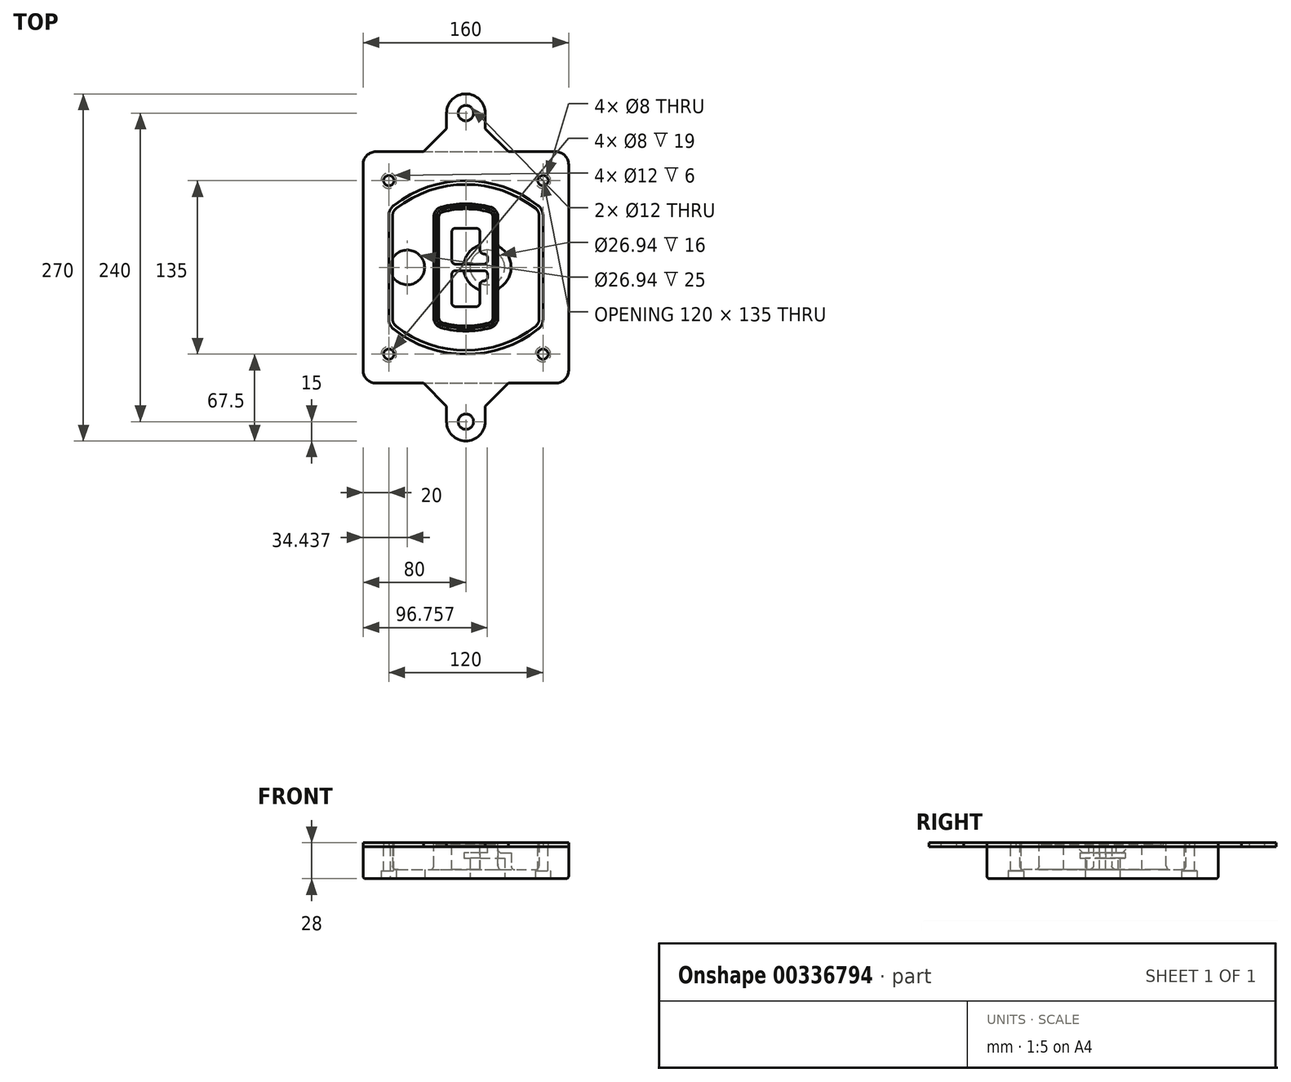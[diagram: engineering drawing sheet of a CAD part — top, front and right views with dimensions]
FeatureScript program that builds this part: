
annotation { "Feature Type Name" : "Feature", "Feature Type Description" : "" }
export const myFeature = defineFeature(function(context is Context, id is Id, definition is map)
    precondition{}
    {
        {
            var Q0;
            Q0=qCreatedBy(makeId("Top.planeOp"),FACE);
            var sketch = newSketch(context, id + "F0", { "sketchPlane" : qUnion([Q0])});
            skPoint(sketch, "E0.rect.middle", {"position": v(0, 0) * mm});
            skLineSegment(sketch, "E1.bottom", {"start": v(-70, -90) * mm, "end": v(70, -90) * mm});
            skLineSegment(sketch, "E1.top", {"start": v(-70, 90) * mm, "end": v(70, 90) * mm});
            skLineSegment(sketch, "E1.left", {"start": v(-80, -80) * mm, "end": v(-80, 80) * mm});
            skLineSegment(sketch, "E1.right", {"start": v(80, -80) * mm, "end": v(80, 80) * mm});
            skLineSegment(sketch, "E2", {"start": v(-80, 90) * mm, "end": v(80, -90) * mm, "construction": true});
            skLineSegment(sketch, "E3", {"start": v(80, 90) * mm, "end": v(-80, -90) * mm, "construction": true});
            skCircle(sketch, "E4", {"center": v(-60, 67.5) * mm, "radius": 4 * mm});
            skCircle(sketch, "E5", {"center": v(60, 67.5) * mm, "radius": 4 * mm});
            skCircle(sketch, "E6", {"center": v(60, -67.5) * mm, "radius": 4 * mm});
            skCircle(sketch, "E7", {"center": v(-60, -67.5) * mm, "radius": 4 * mm});
            skLineSegment(sketch, "E8", {"start": v(-60, 67.5) * mm, "end": v(60, 67.5) * mm, "construction": true});
            skLineSegment(sketch, "E9", {"start": v(60, 67.5) * mm, "end": v(60, -67.5) * mm, "construction": true});
            skLineSegment(sketch, "E10", {"start": v(60, -67.5) * mm, "end": v(-60, -67.5) * mm, "construction": true});
            skLineSegment(sketch, "E11", {"start": v(-60, -67.5) * mm, "end": v(-60, 67.5) * mm, "construction": true});
            skLineSegment(sketch, "E12", {"start": v(-60, 40.3) * mm, "end": v(-60, -40.3) * mm});
            skLineSegment(sketch, "E13", {"start": v(60, 40.3) * mm, "end": v(60, -40.3) * mm});
            skArc(sketch, "E14", {"start": v(56.15, 48.18) * mm, "mid": v(0, 67.5) * mm, "end": v(-56.15, 48.18) * mm});
            skArc(sketch, "E15", {"start": v(-56.15, -48.18) * mm, "mid": v(0, -67.5) * mm, "end": v(56.15, -48.18) * mm});
            skLineSegment(sketch, "E16", {"start": v(-60, 0) * mm, "end": v(60, 0) * mm, "construction": true});
            skPoint(sketch, "E17.visualSharp", {"position": v(-60, -45) * mm});
            skArc(sketch, "E17.filletArc", {"start": v(-60, -40.3) * mm, "mid": v(-58.99, -44.68) * mm, "end": v(-56.15, -48.18) * mm});
            skPoint(sketch, "E18.visualSharp", {"position": v(-60, 45) * mm});
            skArc(sketch, "E18.filletArc", {"start": v(-56.15, 48.18) * mm, "mid": v(-58.99, 44.68) * mm, "end": v(-60, 40.3) * mm});
            skPoint(sketch, "E19.visualSharp", {"position": v(60, 45) * mm});
            skArc(sketch, "E19.filletArc", {"start": v(60, 40.3) * mm, "mid": v(58.99, 44.68) * mm, "end": v(56.15, 48.18) * mm});
            skPoint(sketch, "E20.visualSharp", {"position": v(60, -45) * mm});
            skArc(sketch, "E20.filletArc", {"start": v(56.15, -48.18) * mm, "mid": v(58.99, -44.68) * mm, "end": v(60, -40.3) * mm});
            skPoint(sketch, "E21.visualSharp", {"position": v(-80, 90) * mm});
            skArc(sketch, "E21.filletArc", {"start": v(-70, 90) * mm, "mid": v(-77.07, 87.07) * mm, "end": v(-80, 80) * mm});
            skPoint(sketch, "E22.visualSharp", {"position": v(80, 90) * mm});
            skArc(sketch, "E22.filletArc", {"start": v(80, 80) * mm, "mid": v(77.07, 87.07) * mm, "end": v(70, 90) * mm});
            skPoint(sketch, "E23.visualSharp", {"position": v(80, -90) * mm});
            skArc(sketch, "E23.filletArc", {"start": v(70, -90) * mm, "mid": v(77.07, -87.07) * mm, "end": v(80, -80) * mm});
            skPoint(sketch, "E24.visualSharp", {"position": v(-80, -90) * mm});
            skArc(sketch, "E24.filletArc", {"start": v(-80, -80) * mm, "mid": v(-77.07, -87.07) * mm, "end": v(-70, -90) * mm});
            skArc(sketch, "E25.0", {"start": v(57, 40.3) * mm, "mid": v(56.3, 43.36) * mm, "end": v(54.3, 45.81) * mm});
            skLineSegment(sketch, "E25.1", {"start": v(57, 40.3) * mm, "end": v(57, -40.3) * mm});
            skArc(sketch, "E25.2", {"start": v(54.3, -45.81) * mm, "mid": v(56.3, -43.36) * mm, "end": v(57, -40.3) * mm});
            skArc(sketch, "E25.3", {"start": v(-54.3, -45.81) * mm, "mid": v(0, -64.5) * mm, "end": v(54.3, -45.81) * mm});
            skArc(sketch, "E25.4", {"start": v(-57, -40.3) * mm, "mid": v(-56.3, -43.36) * mm, "end": v(-54.3, -45.81) * mm});
            skArc(sketch, "E25.5", {"start": v(54.3, 45.81) * mm, "mid": v(0, 64.5) * mm, "end": v(-54.3, 45.81) * mm});
            skLineSegment(sketch, "E25.6", {"start": v(-57, 40.3) * mm, "end": v(-57, -40.3) * mm});
            skArc(sketch, "E25.7", {"start": v(-54.3, 45.81) * mm, "mid": v(-56.3, 43.36) * mm, "end": v(-57, 40.3) * mm});
            skArc(sketch, "E26.0", {"start": v(-58.62, 51.33) * mm, "mid": v(-62.58, 46.43) * mm, "end": v(-64, 40.3) * mm});
            skArc(sketch, "E26.1", {"start": v(58.62, 51.33) * mm, "mid": v(0, 71.5) * mm, "end": v(-58.62, 51.33) * mm});
            skArc(sketch, "E26.2", {"start": v(64, 40.3) * mm, "mid": v(62.58, 46.43) * mm, "end": v(58.62, 51.33) * mm});
            skLineSegment(sketch, "E26.3", {"start": v(64, 40.3) * mm, "end": v(64, -40.3) * mm});
            skArc(sketch, "E26.4", {"start": v(58.62, -51.33) * mm, "mid": v(62.58, -46.43) * mm, "end": v(64, -40.3) * mm});
            skLineSegment(sketch, "E26.5", {"start": v(-64, 40.3) * mm, "end": v(-64, -40.3) * mm});
            skArc(sketch, "E26.6", {"start": v(-58.62, -51.33) * mm, "mid": v(0, -71.5) * mm, "end": v(58.62, -51.33) * mm});
            skArc(sketch, "E26.7", {"start": v(-64, -40.3) * mm, "mid": v(-62.58, -46.43) * mm, "end": v(-58.62, -51.33) * mm});
            skSolve(sketch);
        }
        {
            var Q0;
            Q0=makeQuery(id+"F0.imprint","IMPRINT",FACE,{"disambiguationData":[TD([[makeQuery(id+"F0.imprint","IMPRINT",EDGE,{"derivedFrom":sQuery(id+"F0.wireOp",EDGE,"E1.bottom")}),1.0]])]});
            var Q1;
            Q1=makeQuery(id+"F0.imprint","IMPRINT",FACE,{"disambiguationData":[TD([[makeQuery(id+"F0.imprint","IMPRINT",EDGE,{"derivedFrom":sQuery(id+"F0.wireOp",EDGE,"E12")}),1.0]])]});
            var Q2;
            Q2=makeQuery(id+"F0.imprint","IMPRINT",FACE,{"disambiguationData":[TD([[makeQuery(id+"F0.imprint","IMPRINT",EDGE,{"derivedFrom":sQuery(id+"F0.wireOp",EDGE,"E25.0")}),1.0]])]});
            var Q3;
            Q3=makeQuery(id+"F0.imprint","IMPRINT",FACE,{"disambiguationData":[TD([[makeQuery(id+"F0.imprint","IMPRINT",EDGE,{"derivedFrom":sQuery(id+"F0.wireOp",EDGE,"E12")}),-1.0]])]});
            extrude(context, id + "F1", {"entities" : qUnion([Q0, Q1, Q2, Q3]), "oppositeDirection" : true, "depth" : 25 * mm});
        }
        {
            var Q0;
            Q0=makeQuery(id+"F0.imprint","IMPRINT",FACE,{"disambiguationData":[TD([[makeQuery(id+"F0.imprint","IMPRINT",EDGE,{"derivedFrom":sQuery(id+"F0.wireOp",EDGE,"E12")}),1.0]])]});
            extrude(context, id + "F2", {"entities" : qUnion([Q0]), "operationType" : NewBodyOperationType.ADD, "depth" : 3 * mm});
        }
        {
            var Q0;
            Q0=makeQuery(id+"F0.imprint","IMPRINT",FACE,{"disambiguationData":[TD([[makeQuery(id+"F0.imprint","IMPRINT",EDGE,{"derivedFrom":sQuery(id+"F0.wireOp",EDGE,"E25.0")}),1.0]])]});
            extrude(context, id + "F3", {"entities" : qUnion([Q0]), "operationType" : NewBodyOperationType.REMOVE, "oppositeDirection" : true, "depth" : 18 * mm});
        }
        {
            var Q0;
            Q0=makeQuery(id+"F2.opExtrude","CAP_FACE",FACE,{"disambiguationData":[OSD([sQuery(id+"F0.wireOp",EDGE,"E12"),sQuery(id+"F0.wireOp",EDGE,"E13"),sQuery(id+"F0.wireOp",EDGE,"E14"),sQuery(id+"F0.wireOp",EDGE,"E15"),sQuery(id+"F0.wireOp",EDGE,"E17.filletArc"),sQuery(id+"F0.wireOp",EDGE,"E18.filletArc"),sQuery(id+"F0.wireOp",EDGE,"E19.filletArc"),sQuery(id+"F0.wireOp",EDGE,"E20.filletArc"),sQuery(id+"F0.wireOp",EDGE,"E25.0"),sQuery(id+"F0.wireOp",EDGE,"E25.1"),sQuery(id+"F0.wireOp",EDGE,"E25.2"),sQuery(id+"F0.wireOp",EDGE,"E25.3"),sQuery(id+"F0.wireOp",EDGE,"E25.4"),sQuery(id+"F0.wireOp",EDGE,"E25.5"),sQuery(id+"F0.wireOp",EDGE,"E25.6"),sQuery(id+"F0.wireOp",EDGE,"E25.7")])],"isStart":false});
            var sketch = newSketch(context, id + "F4", { "sketchPlane" : qUnion([Q0])});
            skArc(sketch, "E27.0", {"start": v(-19.08, -46.97) * mm, "mid": v(0, -49.5) * mm, "end": v(19.08, -46.97) * mm});
            skArc(sketch, "E28.0", {"start": v(19.08, 46.97) * mm, "mid": v(0, 49.5) * mm, "end": v(-19.08, 46.97) * mm});
            skLineSegment(sketch, "E29", {"start": v(-25, 39.25) * mm, "end": v(-25, -39.25) * mm});
            skLineSegment(sketch, "E30", {"start": v(25, 39.25) * mm, "end": v(25, -39.25) * mm});
            skLineSegment(sketch, "E31", {"start": v(-25, 45.1) * mm, "end": v(25, 45.1) * mm, "construction": true});
            skLineSegment(sketch, "E32", {"start": v(-25, -45.1) * mm, "end": v(25, -45.1) * mm, "construction": true});
            skPoint(sketch, "E33.visualSharp", {"position": v(-25, 45.1) * mm});
            skArc(sketch, "E33.filletArc", {"start": v(-19.08, 46.97) * mm, "mid": v(-23.35, 44.11) * mm, "end": v(-25, 39.25) * mm});
            skPoint(sketch, "E34.visualSharp", {"position": v(25, 45.1) * mm});
            skArc(sketch, "E34.filletArc", {"start": v(25, 39.25) * mm, "mid": v(23.35, 44.11) * mm, "end": v(19.08, 46.97) * mm});
            skPoint(sketch, "E35.visualSharp", {"position": v(25, -45.1) * mm});
            skArc(sketch, "E35.filletArc", {"start": v(19.08, -46.97) * mm, "mid": v(23.35, -44.11) * mm, "end": v(25, -39.25) * mm});
            skPoint(sketch, "E36.visualSharp", {"position": v(-25, -45.1) * mm});
            skArc(sketch, "E36.filletArc", {"start": v(-25, -39.25) * mm, "mid": v(-23.35, -44.11) * mm, "end": v(-19.08, -46.97) * mm});
            skArc(sketch, "E37.0", {"start": v(54.3, 45.81) * mm, "mid": v(0, 64.5) * mm, "end": v(-54.3, 45.81) * mm});
            skArc(sketch, "E37.1", {"start": v(-54.3, 45.81) * mm, "mid": v(-56.3, 43.36) * mm, "end": v(-57, 40.3) * mm});
            skLineSegment(sketch, "E37.2", {"start": v(-57, 40.3) * mm, "end": v(-57, -40.3) * mm});
            skArc(sketch, "E37.3", {"start": v(-57, -40.3) * mm, "mid": v(-56.3, -43.36) * mm, "end": v(-54.3, -45.81) * mm});
            skArc(sketch, "E37.4", {"start": v(-54.3, -45.81) * mm, "mid": v(0, -64.5) * mm, "end": v(54.3, -45.81) * mm});
            skArc(sketch, "E37.5", {"start": v(54.3, -45.81) * mm, "mid": v(56.3, -43.36) * mm, "end": v(57, -40.3) * mm});
            skLineSegment(sketch, "E37.6", {"start": v(57, 40.3) * mm, "end": v(57, -40.3) * mm});
            skArc(sketch, "E37.7", {"start": v(57, 40.3) * mm, "mid": v(56.3, 43.36) * mm, "end": v(54.3, 45.81) * mm});
            skLineSegment(sketch, "E38.0", {"start": v(23, 39.25) * mm, "end": v(23, -39.25) * mm});
            skArc(sketch, "E38.1", {"start": v(18.56, -45.04) * mm, "mid": v(21.76, -42.9) * mm, "end": v(23, -39.25) * mm});
            skArc(sketch, "E38.2", {"start": v(-18.56, -45.04) * mm, "mid": v(0, -47.5) * mm, "end": v(18.56, -45.04) * mm});
            skArc(sketch, "E38.3", {"start": v(-23, -39.25) * mm, "mid": v(-21.76, -42.9) * mm, "end": v(-18.56, -45.04) * mm});
            skLineSegment(sketch, "E38.4", {"start": v(-23, 39.25) * mm, "end": v(-23, -39.25) * mm});
            skArc(sketch, "E38.5", {"start": v(23, 39.25) * mm, "mid": v(21.76, 42.9) * mm, "end": v(18.56, 45.04) * mm});
            skArc(sketch, "E38.6", {"start": v(-18.56, 45.04) * mm, "mid": v(-21.76, 42.9) * mm, "end": v(-23, 39.25) * mm});
            skArc(sketch, "E38.7", {"start": v(18.56, 45.04) * mm, "mid": v(0, 47.5) * mm, "end": v(-18.56, 45.04) * mm});
            skArc(sketch, "E39.0", {"start": v(21, 39.25) * mm, "mid": v(20.18, 41.68) * mm, "end": v(18.04, 43.1) * mm});
            skLineSegment(sketch, "E39.1", {"start": v(21, 39.25) * mm, "end": v(21, -39.25) * mm});
            skArc(sketch, "E39.2", {"start": v(18.04, -43.1) * mm, "mid": v(20.18, -41.68) * mm, "end": v(21, -39.25) * mm});
            skArc(sketch, "E39.3", {"start": v(-18.04, -43.1) * mm, "mid": v(0, -45.5) * mm, "end": v(18.04, -43.1) * mm});
            skArc(sketch, "E39.4", {"start": v(-21, -39.25) * mm, "mid": v(-20.18, -41.68) * mm, "end": v(-18.04, -43.1) * mm});
            skArc(sketch, "E39.5", {"start": v(18.04, 43.1) * mm, "mid": v(0, 45.5) * mm, "end": v(-18.04, 43.1) * mm});
            skLineSegment(sketch, "E39.6", {"start": v(-21, 39.25) * mm, "end": v(-21, -39.25) * mm});
            skArc(sketch, "E39.7", {"start": v(-18.04, 43.1) * mm, "mid": v(-20.18, 41.68) * mm, "end": v(-21, 39.25) * mm});
            skLineSegment(sketch, "E40", {"start": v(-25, 0) * mm, "end": v(25, 0) * mm, "construction": true});
            skLineSegment(sketch, "E41", {"start": v(-11, 5.5) * mm, "end": v(-11, 27.5) * mm});
            skLineSegment(sketch, "E42", {"start": v(-8, 30.5) * mm, "end": v(8, 30.5) * mm});
            skLineSegment(sketch, "E43", {"start": v(11, 27.5) * mm, "end": v(11, 13.5) * mm});
            skLineSegment(sketch, "E44", {"start": v(14, 10.5) * mm, "end": v(14, 10.5) * mm});
            skLineSegment(sketch, "E45", {"start": v(17, 7.5) * mm, "end": v(17, 5.5) * mm});
            skLineSegment(sketch, "E46", {"start": v(14, 2.5) * mm, "end": v(-8, 2.5) * mm});
            skPoint(sketch, "E47.visualSharp", {"position": v(-11, 30.5) * mm});
            skArc(sketch, "E47.filletArc", {"start": v(-8, 30.5) * mm, "mid": v(-10.12, 29.62) * mm, "end": v(-11, 27.5) * mm});
            skPoint(sketch, "E48.visualSharp", {"position": v(11, 30.5) * mm});
            skArc(sketch, "E48.filletArc", {"start": v(11, 27.5) * mm, "mid": v(10.12, 29.62) * mm, "end": v(8, 30.5) * mm});
            skPoint(sketch, "E49.visualSharp", {"position": v(11, 10.5) * mm});
            skArc(sketch, "E49.filletArc", {"start": v(11, 13.5) * mm, "mid": v(11.88, 11.38) * mm, "end": v(14, 10.5) * mm});
            skPoint(sketch, "E50.visualSharp", {"position": v(17, 10.5) * mm});
            skArc(sketch, "E50.filletArc", {"start": v(17, 7.5) * mm, "mid": v(16.12, 9.62) * mm, "end": v(14, 10.5) * mm});
            skPoint(sketch, "E51.visualSharp", {"position": v(17, 2.5) * mm});
            skArc(sketch, "E51.filletArc", {"start": v(14, 2.5) * mm, "mid": v(16.12, 3.38) * mm, "end": v(17, 5.5) * mm});
            skPoint(sketch, "E52.visualSharp", {"position": v(-11, 2.5) * mm});
            skArc(sketch, "E52.filletArc", {"start": v(-11, 5.5) * mm, "mid": v(-10.12, 3.38) * mm, "end": v(-8, 2.5) * mm});
            skLineSegment(sketch, "E53.0.MirrorCS", {"start": v(14, -2.5) * mm, "end": v(-8, -2.5) * mm});
            skArc(sketch, "E54.0.MirrorCS", {"start": v(-11, -5.5) * mm, "mid": v(-10.12, -3.38) * mm, "end": v(-8, -2.5) * mm});
            skLineSegment(sketch, "E55.0.MirrorCS", {"start": v(-11, -5.5) * mm, "end": v(-11, -27.5) * mm});
            skArc(sketch, "E56.0.MirrorCS", {"start": v(-8, -30.5) * mm, "mid": v(-10.12, -29.62) * mm, "end": v(-11, -27.5) * mm});
            skLineSegment(sketch, "E57.0.MirrorCS", {"start": v(-8, -30.5) * mm, "end": v(8, -30.5) * mm});
            skArc(sketch, "E58.0.MirrorCS", {"start": v(11, -27.5) * mm, "mid": v(10.12, -29.62) * mm, "end": v(8, -30.5) * mm});
            skLineSegment(sketch, "E59.0.MirrorCS", {"start": v(11, -27.5) * mm, "end": v(11, -13.5) * mm});
            skArc(sketch, "E60.0.MirrorCS", {"start": v(11, -13.5) * mm, "mid": v(11.88, -11.38) * mm, "end": v(14, -10.5) * mm});
            skArc(sketch, "E61.0.MirrorCS", {"start": v(17, -7.5) * mm, "mid": v(16.12, -9.62) * mm, "end": v(14, -10.5) * mm});
            skLineSegment(sketch, "E62.0.MirrorCS", {"start": v(17, -7.5) * mm, "end": v(17, -5.5) * mm});
            skArc(sketch, "E63.0.MirrorCS", {"start": v(14, -2.5) * mm, "mid": v(16.12, -3.38) * mm, "end": v(17, -5.5) * mm});
            skSolve(sketch);
        }
        {
            var Q0;
            Q0=makeQuery(id+"F4.imprint","IMPRINT",FACE,{"disambiguationData":[TD([[makeQuery(id+"F4.imprint","IMPRINT",EDGE,{"derivedFrom":sQuery(id+"F4.wireOp",EDGE,"E27.0")}),1.0]])]});
            var Q1;
            Q1=makeQuery(id+"F4.imprint","IMPRINT",FACE,{"disambiguationData":[TD([[makeQuery(id+"F4.imprint","IMPRINT",EDGE,{"derivedFrom":sQuery(id+"F4.wireOp",EDGE,"E38.0")}),-1.0]])]});
            var Q2;
            Q2=makeQuery(id+"F4.imprint","IMPRINT",FACE,{"disambiguationData":[TD([[makeQuery(id+"F4.imprint","IMPRINT",EDGE,{"derivedFrom":sQuery(id+"F4.wireOp",EDGE,"E39.0")}),1.0]])]});
            extrude(context, id + "F5", {"entities" : qUnion([Q0, Q1, Q2]), "operationType" : NewBodyOperationType.ADD, "endBound" : BoundingType.UP_TO_NEXT, "oppositeDirection" : true, "depth" : 25 * mm});
        }
        {
            var Q0;
            Q0=makeQuery(id+"F4.imprint","IMPRINT",FACE,{"disambiguationData":[TD([[makeQuery(id+"F4.imprint","IMPRINT",EDGE,{"derivedFrom":sQuery(id+"F4.wireOp",EDGE,"E38.0")}),-1.0]])]});
            extrude(context, id + "F6", {"entities" : qUnion([Q0]), "operationType" : NewBodyOperationType.REMOVE, "oppositeDirection" : true, "depth" : 2 * mm});
        }
        {
            var Q0;
            Q0=makeQuery(id+"F1.opExtrude","CAP_FACE",FACE,{"disambiguationData":[OSD([sQuery(id+"F0.wireOp",EDGE,"E1.bottom"),sQuery(id+"F0.wireOp",EDGE,"E1.top"),sQuery(id+"F0.wireOp",EDGE,"E1.left"),sQuery(id+"F0.wireOp",EDGE,"E1.right"),sQuery(id+"F0.wireOp",EDGE,"E4"),sQuery(id+"F0.wireOp",EDGE,"E5"),sQuery(id+"F0.wireOp",EDGE,"E6"),sQuery(id+"F0.wireOp",EDGE,"E7"),sQuery(id+"F0.wireOp",EDGE,"E21.filletArc"),sQuery(id+"F0.wireOp",EDGE,"E22.filletArc"),sQuery(id+"F0.wireOp",EDGE,"E23.filletArc"),sQuery(id+"F0.wireOp",EDGE,"E24.filletArc")])],"isStart":false});
            var sketch = newSketch(context, id + "F7", { "sketchPlane" : qUnion([Q0])});
            skCircle(sketch, "E64", {"center": v(16.76, 0) * mm, "radius": 13.47 * mm});
            skCircle(sketch, "E65", {"center": v(-45.56, 0) * mm, "radius": 13.47 * mm});
            skLineSegment(sketch, "E66", {"start": v(80, 0) * mm, "end": v(-80, 0) * mm});
            skCircle(sketch, "E67", {"center": v(16.76, 0) * mm, "radius": 18.47 * mm});
            skCircle(sketch, "E68", {"center": v(60, -67.5) * mm, "radius": 6 * mm});
            skCircle(sketch, "E69", {"center": v(-60, -67.5) * mm, "radius": 6 * mm});
            skCircle(sketch, "E70", {"center": v(-60, 67.5) * mm, "radius": 6 * mm});
            skCircle(sketch, "E71", {"center": v(60, 67.5) * mm, "radius": 6 * mm});
            skSolve(sketch);
        }
        {
            var Q0;
            {var subQ1=sQuery(id+"F7.wireOp",EDGE,"E66");var subQ4=sQuery(id+"F7.wireOp",EDGE,"E64");var subQ6=makeQuery(id+"F7.imprint","INTERSECT",VERTEX,{"disambiguationData":[OD(0.0)],"derivedFrom":[subQ4,subQ1]});Q0=makeQuery(id+"F7.imprint","IMPRINT",FACE,{"disambiguationData":[TD([[makeQuery(id+"F7.imprint","IMPRINT",EDGE,{"disambiguationData":[TD([[subQ6,-1.0]])],"derivedFrom":subQ4}),-1.0]])]});}
            var Q1;
            {var subQ0=sQuery(id+"F7.wireOp",EDGE,"E66");var subQ1=sQuery(id+"F7.wireOp",EDGE,"E64");var subQ3=makeQuery(id+"F7.imprint","INTERSECT",VERTEX,{"disambiguationData":[OD(0.0)],"derivedFrom":[subQ1,subQ0]});Q1=makeQuery(id+"F7.imprint","IMPRINT",FACE,{"disambiguationData":[TD([[makeQuery(id+"F7.imprint","IMPRINT",EDGE,{"disambiguationData":[TD([[subQ3,-1.0]])],"derivedFrom":subQ1}),1.0]])]});}
            var Q2;
            {var subQ0=sQuery(id+"F7.wireOp",EDGE,"E66");var subQ1=sQuery(id+"F7.wireOp",EDGE,"E64");var subQ3=makeQuery(id+"F7.imprint","INTERSECT",VERTEX,{"disambiguationData":[OD(0.0)],"derivedFrom":[subQ1,subQ0]});Q2=makeQuery(id+"F7.imprint","IMPRINT",FACE,{"disambiguationData":[TD([[makeQuery(id+"F7.imprint","IMPRINT",EDGE,{"disambiguationData":[TD([[subQ3,1.0]])],"derivedFrom":subQ1}),1.0]])]});}
            var Q3;
            {var subQ1=sQuery(id+"F7.wireOp",EDGE,"E66");var subQ4=sQuery(id+"F7.wireOp",EDGE,"E64");var subQ6=makeQuery(id+"F7.imprint","INTERSECT",VERTEX,{"disambiguationData":[OD(0.0)],"derivedFrom":[subQ4,subQ1]});Q3=makeQuery(id+"F7.imprint","IMPRINT",FACE,{"disambiguationData":[TD([[makeQuery(id+"F7.imprint","IMPRINT",EDGE,{"disambiguationData":[TD([[subQ6,1.0]])],"derivedFrom":subQ4}),-1.0]])]});}
            extrude(context, id + "F8", {"entities" : qUnion([Q0, Q1, Q2, Q3]), "operationType" : NewBodyOperationType.ADD, "oppositeDirection" : true, "depth" : 20 * mm});
        }
        {
            var Q0;
            {var subQ0=sQuery(id+"F7.wireOp",EDGE,"E66");var subQ1=sQuery(id+"F7.wireOp",EDGE,"E64");var subQ3=makeQuery(id+"F7.imprint","INTERSECT",VERTEX,{"disambiguationData":[OD(0.0)],"derivedFrom":[subQ1,subQ0]});Q0=makeQuery(id+"F7.imprint","IMPRINT",FACE,{"disambiguationData":[TD([[makeQuery(id+"F7.imprint","IMPRINT",EDGE,{"disambiguationData":[TD([[subQ3,-1.0]])],"derivedFrom":subQ1}),1.0]])]});}
            var Q1;
            {var subQ0=sQuery(id+"F7.wireOp",EDGE,"E66");var subQ1=sQuery(id+"F7.wireOp",EDGE,"E64");var subQ3=makeQuery(id+"F7.imprint","INTERSECT",VERTEX,{"disambiguationData":[OD(0.0)],"derivedFrom":[subQ1,subQ0]});Q1=makeQuery(id+"F7.imprint","IMPRINT",FACE,{"disambiguationData":[TD([[makeQuery(id+"F7.imprint","IMPRINT",EDGE,{"disambiguationData":[TD([[subQ3,1.0]])],"derivedFrom":subQ1}),1.0]])]});}
            extrude(context, id + "F9", {"entities" : qUnion([Q0, Q1]), "operationType" : NewBodyOperationType.REMOVE, "oppositeDirection" : true, "depth" : 16 * mm});
        }
        {
            var Q0;
            {var subQ0=sQuery(id+"F7.wireOp",EDGE,"E66");var subQ1=sQuery(id+"F7.wireOp",EDGE,"E65");var subQ3=makeQuery(id+"F7.imprint","INTERSECT",VERTEX,{"disambiguationData":[OD(0.0)],"derivedFrom":[subQ1,subQ0]});Q0=makeQuery(id+"F7.imprint","IMPRINT",FACE,{"disambiguationData":[TD([[makeQuery(id+"F7.imprint","IMPRINT",EDGE,{"disambiguationData":[TD([[subQ3,-1.0]])],"derivedFrom":subQ1}),1.0]])]});}
            var Q1;
            {var subQ0=sQuery(id+"F7.wireOp",EDGE,"E66");var subQ1=sQuery(id+"F7.wireOp",EDGE,"E65");var subQ3=makeQuery(id+"F7.imprint","INTERSECT",VERTEX,{"disambiguationData":[OD(0.0)],"derivedFrom":[subQ1,subQ0]});Q1=makeQuery(id+"F7.imprint","IMPRINT",FACE,{"disambiguationData":[TD([[makeQuery(id+"F7.imprint","IMPRINT",EDGE,{"disambiguationData":[TD([[subQ3,1.0]])],"derivedFrom":subQ1}),1.0]])]});}
            extrude(context, id + "F10", {"entities" : qUnion([Q0, Q1]), "operationType" : NewBodyOperationType.REMOVE, "oppositeDirection" : true, "depth" : 25 * mm});
        }
        {
            var Q0;
            Q0=makeQuery(id+"F7.imprint","IMPRINT",FACE,{"disambiguationData":[TD([[makeQuery(id+"F7.imprint","IMPRINT",EDGE,{"derivedFrom":sQuery(id+"F7.wireOp",EDGE,"E68")}),1.0]])]});
            var Q1;
            Q1=makeQuery(id+"F7.imprint","IMPRINT",FACE,{"disambiguationData":[TD([[makeQuery(id+"F7.imprint","IMPRINT",EDGE,{"derivedFrom":makeQuery(id+"F1.opExtrude","CAP_EDGE",EDGE,{"disambiguationData":[OSD([sQuery(id+"F0.wireOp",EDGE,"E5")])],"isStart":false})}),-1.0]])]});
            var Q2;
            Q2=makeQuery(id+"F7.imprint","IMPRINT",FACE,{"disambiguationData":[TD([[makeQuery(id+"F7.imprint","IMPRINT",EDGE,{"derivedFrom":sQuery(id+"F7.wireOp",EDGE,"E69")}),1.0]])]});
            var Q3;
            Q3=makeQuery(id+"F7.imprint","IMPRINT",FACE,{"disambiguationData":[TD([[makeQuery(id+"F7.imprint","IMPRINT",EDGE,{"derivedFrom":makeQuery(id+"F1.opExtrude","CAP_EDGE",EDGE,{"disambiguationData":[OSD([sQuery(id+"F0.wireOp",EDGE,"E4")])],"isStart":false})}),-1.0]])]});
            var Q4;
            Q4=makeQuery(id+"F7.imprint","IMPRINT",FACE,{"disambiguationData":[TD([[makeQuery(id+"F7.imprint","IMPRINT",EDGE,{"derivedFrom":sQuery(id+"F7.wireOp",EDGE,"E70")}),1.0]])]});
            var Q5;
            Q5=makeQuery(id+"F7.imprint","IMPRINT",FACE,{"disambiguationData":[TD([[makeQuery(id+"F7.imprint","IMPRINT",EDGE,{"derivedFrom":makeQuery(id+"F1.opExtrude","CAP_EDGE",EDGE,{"disambiguationData":[OSD([sQuery(id+"F0.wireOp",EDGE,"E7")])],"isStart":false})}),-1.0]])]});
            var Q6;
            Q6=makeQuery(id+"F7.imprint","IMPRINT",FACE,{"disambiguationData":[TD([[makeQuery(id+"F7.imprint","IMPRINT",EDGE,{"derivedFrom":sQuery(id+"F7.wireOp",EDGE,"E71")}),1.0]])]});
            var Q7;
            Q7=makeQuery(id+"F7.imprint","IMPRINT",FACE,{"disambiguationData":[TD([[makeQuery(id+"F7.imprint","IMPRINT",EDGE,{"derivedFrom":makeQuery(id+"F1.opExtrude","CAP_EDGE",EDGE,{"disambiguationData":[OSD([sQuery(id+"F0.wireOp",EDGE,"E6")])],"isStart":false})}),-1.0]])]});
            extrude(context, id + "F11", {"entities" : qUnion([Q0, Q1, Q2, Q3, Q4, Q5, Q6, Q7]), "operationType" : NewBodyOperationType.REMOVE, "oppositeDirection" : true, "depth" : 6 * mm});
        }
        {
            var Q0;
            Q0=makeQuery(id+"F9.boolean.opBoolean","COPY",FACE,{"derivedFrom":makeQuery(id+"F9.opExtrude","CAP_FACE",FACE,{"disambiguationData":[OSD([sQuery(id+"F7.wireOp",EDGE,"E64")])],"isStart":false})});
            var sketch = newSketch(context, id + "F12", { "sketchPlane" : qUnion([Q0])});
            skArc(sketch, "E72.0", {"start": v(11, 17.55) * mm, "mid": v(2.57, 11.82) * mm, "end": v(-1.54, 2.5) * mm});
            skArc(sketch, "E72.1", {"start": v(-1.54, -2.5) * mm, "mid": v(2.57, -11.82) * mm, "end": v(11, -17.55) * mm});
            skLineSegment(sketch, "E73", {"start": v(-1.54, -2.5) * mm, "end": v(14, -2.5) * mm});
            skLineSegment(sketch, "E74.0", {"start": v(14, 2.5) * mm, "end": v(-1.54, 2.5) * mm});
            skArc(sketch, "E74.1", {"start": v(14, 2.5) * mm, "mid": v(16.12, 3.38) * mm, "end": v(17, 5.5) * mm});
            skLineSegment(sketch, "E74.2", {"start": v(17, 7.5) * mm, "end": v(17, 5.5) * mm});
            skArc(sketch, "E74.3", {"start": v(17, 7.5) * mm, "mid": v(16.12, 9.62) * mm, "end": v(14, 10.5) * mm});
            skArc(sketch, "E74.4", {"start": v(11, 13.5) * mm, "mid": v(11.88, 11.38) * mm, "end": v(14, 10.5) * mm});
            skLineSegment(sketch, "E74.5", {"start": v(11, 17.55) * mm, "end": v(11, 13.5) * mm});
            skLineSegment(sketch, "E74.7", {"start": v(14, -2.5) * mm, "end": v(-1.54, -2.5) * mm});
            skArc(sketch, "E74.8", {"start": v(14, -2.5) * mm, "mid": v(16.12, -3.38) * mm, "end": v(17, -5.5) * mm});
            skLineSegment(sketch, "E74.9", {"start": v(17, -7.5) * mm, "end": v(17, -5.5) * mm});
            skArc(sketch, "E74.10", {"start": v(17, -7.5) * mm, "mid": v(16.12, -9.62) * mm, "end": v(14, -10.5) * mm});
            skArc(sketch, "E74.11", {"start": v(11, -13.5) * mm, "mid": v(11.88, -11.38) * mm, "end": v(14, -10.5) * mm});
            skLineSegment(sketch, "E74.12", {"start": v(11, -17.55) * mm, "end": v(11, -13.5) * mm});
            skPoint(sketch, "E75.orphan", {"position": v(11, -27.5) * mm});
            skPoint(sketch, "E76.orphan", {"position": v(-8, -2.5) * mm});
            skPoint(sketch, "E77.orphan", {"position": v(-8, 2.5) * mm});
            skPoint(sketch, "E78.orphan", {"position": v(11, 27.5) * mm});
            skSolve(sketch);
        }
        {
            var Q0;
            {var subQ7=sQuery(id+"F12.wireOp",EDGE,"E72.0");var subQ14=sQuery(id+"F12.wireOp",EDGE,"E72.1");var subQ16=sQuery(id+"F12.wireOp",EDGE,"E74.1");var subQ18=sQuery(id+"F12.wireOp",EDGE,"E74.8");Q0=qUnion([makeQuery(id+"F12.imprint","IMPRINT",FACE,{"disambiguationData":[TD([[makeQuery(id+"F12.imprint","IMPRINT",EDGE,{"derivedFrom":subQ7}),1.0]])]}),makeQuery(id+"F12.imprint","IMPRINT",FACE,{"disambiguationData":[TD([[makeQuery(id+"F12.imprint","IMPRINT",EDGE,{"derivedFrom":subQ14}),1.0]])]}),makeQuery(id+"F12.imprint","IMPRINT",FACE,{"disambiguationData":[TD([[makeQuery(id+"F12.imprint","IMPRINT",EDGE,{"derivedFrom":subQ16}),1.0]])]}),makeQuery(id+"F12.imprint","IMPRINT",FACE,{"disambiguationData":[TD([[makeQuery(id+"F12.imprint","IMPRINT",EDGE,{"derivedFrom":subQ18}),-1.0]])]})]);}
            var Q1;
            Q1=makeQuery(id+"F5.boolean.opBoolean","SPLIT",FACE,{"disambiguationData":[TD([makeQuery(id+"F5.opExtrude","SWEPT_FACE",FACE,{"disambiguationData":[OSD([sQuery(id+"F4.wireOp",EDGE,"E41")])]})])],"derivedFrom":makeQuery(id+"F3.boolean.opBoolean","COPY",FACE,{"derivedFrom":makeQuery(id+"F3.opExtrude","CAP_FACE",FACE,{"disambiguationData":[OSD([sQuery(id+"F0.wireOp",EDGE,"E25.0"),sQuery(id+"F0.wireOp",EDGE,"E25.1"),sQuery(id+"F0.wireOp",EDGE,"E25.2"),sQuery(id+"F0.wireOp",EDGE,"E25.3"),sQuery(id+"F0.wireOp",EDGE,"E25.4"),sQuery(id+"F0.wireOp",EDGE,"E25.5"),sQuery(id+"F0.wireOp",EDGE,"E25.6"),sQuery(id+"F0.wireOp",EDGE,"E25.7")])],"isStart":false})})});
            extrude(context, id + "F13", {"entities" : qUnion([Q0]), "operationType" : NewBodyOperationType.REMOVE, "endBound" : BoundingType.UP_TO_SURFACE, "endBoundEntityFace" : qUnion([Q1]), "depth" : 25 * mm});
        }
        {
            var Q0;
            Q0=makeQuery(id+"F3.boolean.opBoolean","COPY",EDGE,{"derivedFrom":makeQuery(id+"F3.opExtrude","CAP_EDGE",EDGE,{"disambiguationData":[OSD([sQuery(id+"F0.wireOp",EDGE,"E25.6")])],"isStart":false})});
            var Q1;
            Q1=makeQuery(id+"F8.boolean.opBoolean","INTERSECT",EDGE,{"derivedFrom":[makeQuery(id+"F5.opExtrude","SWEPT_FACE",FACE,{"disambiguationData":[OSD([sQuery(id+"F4.wireOp",EDGE,"E30")])]}),makeQuery(id+"F8.opExtrude","CAP_FACE",FACE,{"disambiguationData":[OSD([sQuery(id+"F7.wireOp",EDGE,"E67")])],"isStart":false})]});
            var Q2;
            Q2=makeQuery(id+"F8.boolean.opBoolean","INTERSECT",EDGE,{"disambiguationData":[OD(1.0)],"derivedFrom":[makeQuery(id+"F5.opExtrude","SWEPT_FACE",FACE,{"disambiguationData":[OSD([sQuery(id+"F4.wireOp",EDGE,"E30")])]}),makeQuery(id+"F8.opExtrude","SWEPT_FACE",FACE,{"disambiguationData":[OSD([sQuery(id+"F7.wireOp",EDGE,"E67")])]})]});
            var Q3;
            {var subQ0=sQuery(id+"F4.wireOp",EDGE,"E30");Q3=makeQuery(id+"F8.boolean.opBoolean","SPLIT",EDGE,{"disambiguationData":[TD([makeQuery(id+"F5.opExtrude","SWEPT_FACE",FACE,{"disambiguationData":[OSD([sQuery(id+"F4.wireOp",EDGE,"E35.filletArc")])]})])],"derivedFrom":makeQuery(id+"F5.opExtrude","CAP_EDGE",EDGE,{"disambiguationData":[OSD([subQ0])],"isStart":false})});}
            var Q4;
            {var subQ0=sQuery(id+"F0.wireOp",EDGE,"E25.7");var subQ1=sQuery(id+"F0.wireOp",EDGE,"E25.1");var subQ2=sQuery(id+"F0.wireOp",EDGE,"E25.6");var subQ3=sQuery(id+"F0.wireOp",EDGE,"E25.5");var subQ4=sQuery(id+"F0.wireOp",EDGE,"E25.4");var subQ5=sQuery(id+"F0.wireOp",EDGE,"E25.0");var subQ6=sQuery(id+"F0.wireOp",EDGE,"E25.2");var subQ7=sQuery(id+"F0.wireOp",EDGE,"E25.3");Q4=makeQuery(id+"F8.boolean.opBoolean","INTERSECT",EDGE,{"derivedFrom":[makeQuery(id+"F5.boolean.opBoolean","SPLIT",FACE,{"disambiguationData":[TD([makeQuery(id+"F2.opExtrude","SWEPT_FACE",FACE,{"disambiguationData":[OSD([subQ5])]})])],"derivedFrom":makeQuery(id+"F3.boolean.opBoolean","COPY",FACE,{"derivedFrom":makeQuery(id+"F3.opExtrude","CAP_FACE",FACE,{"disambiguationData":[OSD([subQ5,subQ1,subQ6,subQ7,subQ4,subQ3,subQ2,subQ0])],"isStart":false})})}),makeQuery(id+"F8.opExtrude","SWEPT_FACE",FACE,{"disambiguationData":[OSD([sQuery(id+"F7.wireOp",EDGE,"E67")])]})]});}
            var Q5;
            Q5=makeQuery(id+"F8.boolean.opBoolean","INTERSECT",EDGE,{"disambiguationData":[OD(0.0)],"derivedFrom":[makeQuery(id+"F5.opExtrude","SWEPT_FACE",FACE,{"disambiguationData":[OSD([sQuery(id+"F4.wireOp",EDGE,"E30")])]}),makeQuery(id+"F8.opExtrude","SWEPT_FACE",FACE,{"disambiguationData":[OSD([sQuery(id+"F7.wireOp",EDGE,"E67")])]})]});
            fillet(context, id + "F14", {"entities" : qUnion([Q0, Q1, Q2, Q3, Q4, Q5]), "radius" : 3 * mm, "tangentPropagation" : true, "allowEdgeOverflow" : false});
        }
        {
            var Q0;
            Q0=makeQuery(id+"F1.opExtrude","CAP_EDGE",EDGE,{"disambiguationData":[OSD([sQuery(id+"F0.wireOp",EDGE,"E1.bottom")])],"isStart":false});
            fillet(context, id + "F15", {"entities" : qUnion([Q0]), "radius" : 2 * mm, "tangentPropagation" : true, "allowEdgeOverflow" : false});
        }
        {
            var Q0;
            Q0=qCreatedBy(makeId("Top.planeOp"),FACE);
            var sketch = newSketch(context, id + "F16", { "sketchPlane" : qUnion([Q0])});
            skCircle(sketch, "E79.0", {"center": v(-60, 67.5) * mm, "radius": 4 * mm});
            skCircle(sketch, "E79.1", {"center": v(60, 67.5) * mm, "radius": 4 * mm});
            skCircle(sketch, "E79.2", {"center": v(60, -67.5) * mm, "radius": 4 * mm});
            skCircle(sketch, "E79.3", {"center": v(-60, -67.5) * mm, "radius": 4 * mm});
            skArc(sketch, "E79.4", {"start": v(-56.15, -48.18) * mm, "mid": v(0, -67.5) * mm, "end": v(56.15, -48.18) * mm});
            skArc(sketch, "E79.5", {"start": v(-60, -40.3) * mm, "mid": v(-58.99, -44.68) * mm, "end": v(-56.15, -48.18) * mm});
            skLineSegment(sketch, "E79.6", {"start": v(-60, 40.3) * mm, "end": v(-60, -40.3) * mm});
            skArc(sketch, "E79.7", {"start": v(-56.15, 48.18) * mm, "mid": v(-58.99, 44.68) * mm, "end": v(-60, 40.3) * mm});
            skArc(sketch, "E79.8", {"start": v(56.15, 48.18) * mm, "mid": v(0, 67.5) * mm, "end": v(-56.15, 48.18) * mm});
            skArc(sketch, "E79.9", {"start": v(60, 40.3) * mm, "mid": v(58.99, 44.68) * mm, "end": v(56.15, 48.18) * mm});
            skLineSegment(sketch, "E79.10", {"start": v(60, 40.3) * mm, "end": v(60, -40.3) * mm});
            skArc(sketch, "E79.11", {"start": v(56.15, -48.18) * mm, "mid": v(58.99, -44.68) * mm, "end": v(60, -40.3) * mm});
            skLineSegment(sketch, "E79.12", {"start": v(80, -80) * mm, "end": v(80, 80) * mm});
            skArc(sketch, "E79.13", {"start": v(80, 80) * mm, "mid": v(77.07, 87.07) * mm, "end": v(70, 90) * mm});
            skLineSegment(sketch, "E79.14", {"start": v(-70, 90) * mm, "end": v(70, 90) * mm});
            skArc(sketch, "E79.15", {"start": v(-70, 90) * mm, "mid": v(-77.07, 87.07) * mm, "end": v(-80, 80) * mm});
            skLineSegment(sketch, "E79.16", {"start": v(-80, -80) * mm, "end": v(-80, 80) * mm});
            skArc(sketch, "E79.17", {"start": v(-80, -80) * mm, "mid": v(-77.07, -87.07) * mm, "end": v(-70, -90) * mm});
            skLineSegment(sketch, "E79.18", {"start": v(-70, -90) * mm, "end": v(70, -90) * mm});
            skArc(sketch, "E79.19", {"start": v(70, -90) * mm, "mid": v(77.07, -87.07) * mm, "end": v(80, -80) * mm});
            skPoint(sketch, "E80.endSnap0", {"position": v(0, 90) * mm});
            skLineSegment(sketch, "E81", {"start": v(0, 90) * mm, "end": v(0, 120) * mm, "construction": true});
            skLineSegment(sketch, "E82", {"start": v(-33, 90) * mm, "end": v(-15, 108) * mm});
            skLineSegment(sketch, "E83", {"start": v(15, 108) * mm, "end": v(33, 90) * mm});
            skLineSegment(sketch, "E84", {"start": v(15, 108) * mm, "end": v(15, 120) * mm});
            skLineSegment(sketch, "E85", {"start": v(-15, 108) * mm, "end": v(-15, 120) * mm});
            skArc(sketch, "E86", {"start": v(15, 120) * mm, "mid": v(0, 135) * mm, "end": v(-15, 120) * mm});
            skCircle(sketch, "E87", {"center": v(0, 120) * mm, "radius": 6 * mm});
            skLineSegment(sketch, "E88", {"start": v(-80, 0) * mm, "end": v(80, 0) * mm, "construction": true});
            skLineSegment(sketch, "E89.MirrorCS", {"start": v(-33, -90) * mm, "end": v(-15, -108) * mm});
            skPoint(sketch, "E90.MirrorP", {"position": v(0, -90) * mm});
            skLineSegment(sketch, "E91.MirrorCS", {"start": v(0, -90) * mm, "end": v(0, -120) * mm, "construction": true});
            skCircle(sketch, "E92.MirrorC", {"center": v(0, -120) * mm, "radius": 6 * mm});
            skLineSegment(sketch, "E93.MirrorCS", {"start": v(-15, -108) * mm, "end": v(-15, -120) * mm});
            skArc(sketch, "E94.MirrorCS", {"start": v(15, -120) * mm, "mid": v(0, -135) * mm, "end": v(-15, -120) * mm});
            skLineSegment(sketch, "E95.MirrorCS", {"start": v(15, -108) * mm, "end": v(15, -120) * mm});
            skLineSegment(sketch, "E96.MirrorCS", {"start": v(15, -108) * mm, "end": v(33, -90) * mm});
            skSolve(sketch);
        }
        {
            var Q0;
            Q0 = qSketchRegion(id + "F16", true);
            var Q1;
            Q1=makeQuery(id+"F2.opExtrude","CAP_FACE",FACE,{"disambiguationData":[OSD([sQuery(id+"F0.wireOp",EDGE,"E12"),sQuery(id+"F0.wireOp",EDGE,"E13"),sQuery(id+"F0.wireOp",EDGE,"E14"),sQuery(id+"F0.wireOp",EDGE,"E15"),sQuery(id+"F0.wireOp",EDGE,"E17.filletArc"),sQuery(id+"F0.wireOp",EDGE,"E18.filletArc"),sQuery(id+"F0.wireOp",EDGE,"E19.filletArc"),sQuery(id+"F0.wireOp",EDGE,"E20.filletArc"),sQuery(id+"F0.wireOp",EDGE,"E25.0"),sQuery(id+"F0.wireOp",EDGE,"E25.1"),sQuery(id+"F0.wireOp",EDGE,"E25.2"),sQuery(id+"F0.wireOp",EDGE,"E25.3"),sQuery(id+"F0.wireOp",EDGE,"E25.4"),sQuery(id+"F0.wireOp",EDGE,"E25.5"),sQuery(id+"F0.wireOp",EDGE,"E25.6"),sQuery(id+"F0.wireOp",EDGE,"E25.7")])],"isStart":false});
            extrude(context, id + "F17", {"entities" : qUnion([Q0]), "endBound" : BoundingType.UP_TO_SURFACE, "endBoundEntityFace" : qUnion([Q1]), "depth" : 25 * mm});
        }
    });
